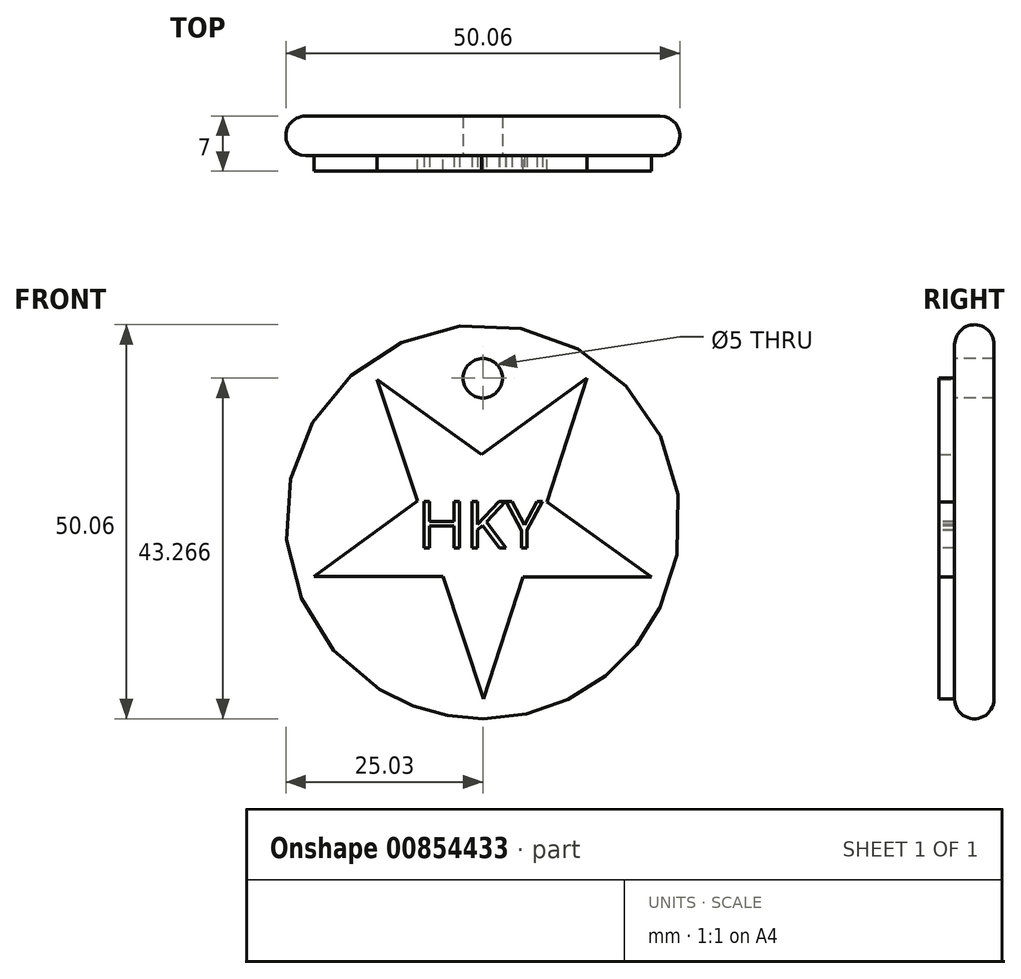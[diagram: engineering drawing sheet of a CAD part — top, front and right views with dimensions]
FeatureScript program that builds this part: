
annotation { "Feature Type Name" : "Feature", "Feature Type Description" : "" }
export const myFeature = defineFeature(function(context is Context, id is Id, definition is map)
    precondition{}
    {
        {
            var Q0;
            Q0=qCreatedBy(makeId("Front.planeOp"),FACE);
            var sketch = newSketch(context, id + "F0", { "sketchPlane" : qUnion([Q0])});
            skCircle(sketch, "E0", {"center": v(0, 0) * mm, "radius": 25.03 * mm});
            skSolve(sketch);
        }
        {
            var Q0;
            Q0=makeQuery(id+"F0.imprint","IMPRINT",FACE,{"disambiguationData":[TD([[makeQuery(id+"F0.imprint","IMPRINT",EDGE,{"derivedFrom":sQuery(id+"F0.wireOp",EDGE,"E0")}),1.0]])]});
            extrude(context, id + "F1", {"entities" : qUnion([Q0]), "depth" : 2.5 * mm, "offsetDistance" : 25 * mm, "hasSecondDirection" : true, "secondDirectionOppositeDirection" : true, "secondDirectionDepth" : 2.5 * mm});
        }
        {
            var Q0;
            Q0=makeQuery(id+"F1.opExtrude","SWEPT_FACE",FACE,{"disambiguationData":[OSD([sQuery(id+"F0.wireOp",EDGE,"E0")])]});
            var Q1;
            Q1=makeQuery(id+"F1.opExtrude","CAP_FACE",FACE,{"disambiguationData":[OSD([sQuery(id+"F0.wireOp",EDGE,"E0")])],"isStart":false});
            var Q2;
            Q2=makeQuery(id+"F1.opExtrude","CAP_FACE",FACE,{"disambiguationData":[OSD([sQuery(id+"F0.wireOp",EDGE,"E0")])],"isStart":true});
            fillet(context, id + "F2", {"entities" : qUnion([Q0, Q1, Q2]), "radius" : 2.5 * mm, "tangentPropagation" : true, "allowEdgeOverflow" : false});
        }
        {
            var Q0;
            Q0=makeQuery(id+"F1.opExtrude","CAP_FACE",FACE,{"disambiguationData":[OSD([sQuery(id+"F0.wireOp",EDGE,"E0")])],"isStart":false});
            var sketch = newSketch(context, id + "F3", { "sketchPlane" : qUnion([Q0])});
            skPoint(sketch, "E1.0.midPoint", {"position": v(0, 18.6) * mm});
            skLineSegment(sketch, "E2", {"start": v(-13.45, 18.07) * mm, "end": v(0.1, -22.53) * mm});
            skLineSegment(sketch, "E3", {"start": v(0.1, -22.53) * mm, "end": v(13.2, 18.26) * mm});
            skLineSegment(sketch, "E4", {"start": v(13.2, 18.26) * mm, "end": v(-21.43, -6.93) * mm});
            skLineSegment(sketch, "E5", {"start": v(-21.43, -6.93) * mm, "end": v(21.4, -7.04) * mm});
            skLineSegment(sketch, "E6", {"start": v(21.4, -7.04) * mm, "end": v(-13.45, 18.07) * mm});
            skSolve(sketch);
        }
        {
            var Q0;
            Q0 = qSketchRegion(id + "F3", true);
            extrude(context, id + "F4", {"entities" : qUnion([Q0]), "operationType" : NewBodyOperationType.ADD, "depth" : 2 * mm, "offsetDistance" : 25 * mm});
        }
        {
            var Q0;
            {var subQ0=sQuery(id+"F3.wireOp",EDGE,"E4");var subQ1=sQuery(id+"F3.wireOp",EDGE,"E3");var subQ2=sQuery(id+"F0.wireOp",EDGE,"E0");var subQ3=makeQuery(id+"F1.opExtrude","CAP_FACE",FACE,{"disambiguationData":[OSD([subQ2])],"isStart":false});var subQ6=sQuery(id+"F3.wireOp",EDGE,"E6");var subQ7=sQuery(id+"F3.wireOp",EDGE,"E2");var subQ9=makeQuery(id+"F3.imprint","INTERSECT",VERTEX,{"derivedFrom":[subQ0,subQ6]});Q0=makeQuery(id+"F4.boolean.opBoolean","SPLIT",FACE,{"disambiguationData":[TD([subQ3,makeQuery(id+"F2.opFillet","BLEND_FACE",FACE,{"disambiguationData":[OSD([subQ2])]}),makeQuery(id+"F4.opExtrude","SWEPT_FACE",FACE,{"disambiguationData":[OSD([subQ7]),TDD([makeQuery(id+"F3.imprint","IMPRINT",EDGE,{"disambiguationData":[TD([[makeQuery(id+"F3.imprint","INTERSECT",VERTEX,{"derivedFrom":[subQ7,subQ0]}),1.0]])],"derivedFrom":subQ7})])]}),makeQuery(id+"F4.opExtrude","SWEPT_FACE",FACE,{"disambiguationData":[OSD([subQ1]),TDD([makeQuery(id+"F3.imprint","IMPRINT",EDGE,{"disambiguationData":[TD([[makeQuery(id+"F3.imprint","INTERSECT",VERTEX,{"derivedFrom":[subQ1,subQ6]}),-1.0]])],"derivedFrom":subQ1})])]}),makeQuery(id+"F4.opExtrude","SWEPT_FACE",FACE,{"disambiguationData":[OSD([subQ0]),TDD([makeQuery(id+"F3.imprint","IMPRINT",EDGE,{"disambiguationData":[TD([[subQ9,1.0]])],"derivedFrom":subQ0})])]}),makeQuery(id+"F4.opExtrude","SWEPT_FACE",FACE,{"disambiguationData":[OSD([subQ6]),TDD([makeQuery(id+"F3.imprint","IMPRINT",EDGE,{"disambiguationData":[TD([[subQ9,-1.0]])],"derivedFrom":subQ6})])]})])],"derivedFrom":subQ3});}
            var sketch = newSketch(context, id + "F5", { "sketchPlane" : qUnion([Q0])});
            skCircle(sketch, "E7", {"center": v(0, 18.24) * mm, "radius": 2.07 * mm});
            skSolve(sketch);
        }
        {
            var Q0;
            Q0=sQuery(id+"F5.wireOp",VERTEX,"E7.center");
            var Q1;
            Q1=makeQuery(id+"F1.opExtrude","SWEPT_BODY",BODY,{"disambiguationData":[OSD([sQuery(id+"F0.wireOp",EDGE,"E0")])]});
            hole(context, id + "F6", {"style" : HoleStyle.SIMPLE, "endStyle" : HoleEndStyle.THROUGH, "holeDiameter" : 5 * mm, "majorDiameter" : 5 * mm, "isTappedThrough" : true, "tappedDepth" : 12 * mm, "tapClearance" : 3, "locations" : qUnion([Q0]), "scope" : qUnion([Q1])});
        }
        {
            var Q0;
            Q0=makeQuery(id+"F4.opExtrude","CAP_FACE",FACE,{"disambiguationData":[OSD([sQuery(id+"F3.wireOp",EDGE,"E2"),sQuery(id+"F3.wireOp",EDGE,"E3"),sQuery(id+"F3.wireOp",EDGE,"E4"),sQuery(id+"F3.wireOp",EDGE,"E5"),sQuery(id+"F3.wireOp",EDGE,"E6")])],"isStart":false});
            var sketch = newSketch(context, id + "F7", { "sketchPlane" : qUnion([Q0])});
            skText(sketch, "E8", { "text": "HKY", "fontName": "OpenSans-Regular.ttf"});
            const initialGuessF7  = {"E8": [-0.0083, -0.00336, 1, 0, 0.00599]};
            skSetInitialGuess(sketch, initialGuessF7);
            skSolve(sketch);
        }
        {
            var Q0;
            Q0 = qSketchRegion(id + "F7", true);
            extrude(context, id + "F8", {"entities" : qUnion([Q0]), "oppositeDirection" : true, "depth" : 2 * mm, "offsetDistance" : 25 * mm});
        }
    });
